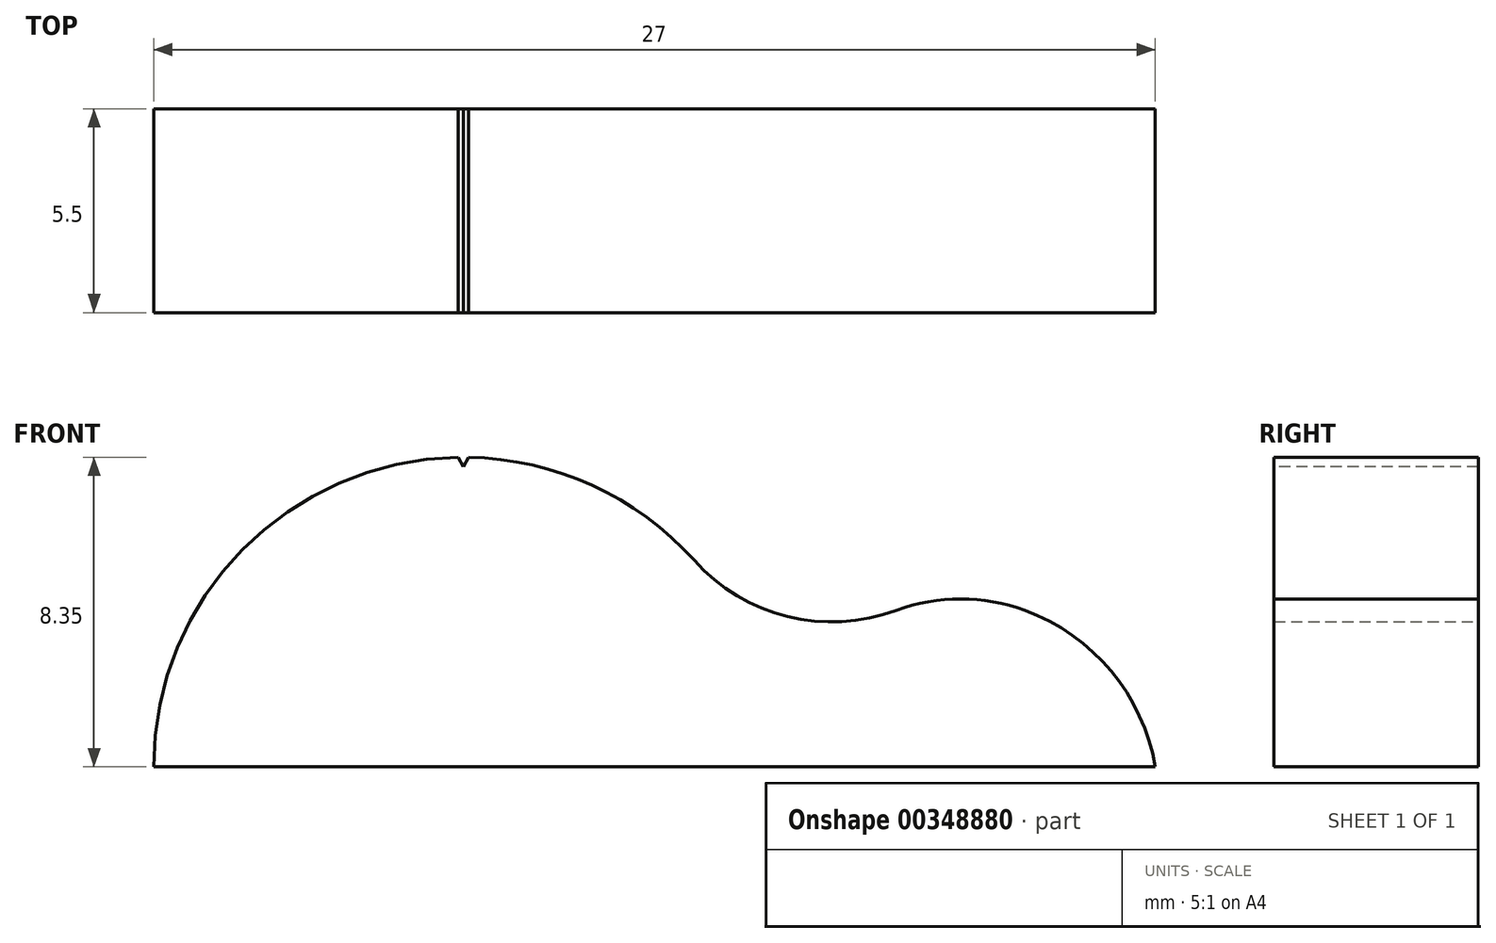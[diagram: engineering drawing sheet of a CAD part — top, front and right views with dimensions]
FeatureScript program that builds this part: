
annotation { "Feature Type Name" : "Feature", "Feature Type Description" : "" }
export const myFeature = defineFeature(function(context is Context, id is Id, definition is map)
    precondition{}
    {
        {
            var Q0;
            Q0=qCreatedBy(makeId("Front.planeOp"),FACE);
            var sketch = newSketch(context, id + "F0", { "sketchPlane" : qUnion([Q0])});
            skLineSegment(sketch, "E0", {"start": v(0, 0) * mm, "end": v(-27, 0) * mm});
            skArc(sketch, "E1", {"start": v(-27, 0) * mm, "mid": v(-21.63, 7.8) * mm, "end": v(-12.43, 5.57) * mm});
            skArc(sketch, "E2", {"start": v(-12.43, 5.57) * mm, "mid": v(-9.91, 4.06) * mm, "end": v(-6.98, 4.22) * mm});
            skArc(sketch, "E3", {"start": v(-3.51, 4.22) * mm, "mid": v(-5.25, 4.53) * mm, "end": v(-6.98, 4.22) * mm});
            skArc(sketch, "E4", {"start": v(0, 0) * mm, "mid": v(-1.2, 2.58) * mm, "end": v(-3.51, 4.22) * mm});
            skSolve(sketch);
        }
        {
            var Q0;
            Q0=qSketchRegion(id+"F0",true);
            extrude(context, id + "F1", {"entities" : qUnion([Q0]), "depth" : 5.5 * mm});
        }
        {
            var Q0;
            Q0=makeQuery(id+"F1.opExtrude","CAP_FACE",FACE,{"disambiguationData":[OSD([sQuery(id+"F0.wireOp",EDGE,"E0"),sQuery(id+"F0.wireOp",EDGE,"E1"),sQuery(id+"F0.wireOp",EDGE,"E2"),sQuery(id+"F0.wireOp",EDGE,"E3"),sQuery(id+"F0.wireOp",EDGE,"E4")])],"isStart":false});
            var sketch = newSketch(context, id + "F2", { "sketchPlane" : qUnion([Q0])});
            skArc(sketch, "E5.0", {"start": v(-18.8, 8.35) * mm, "mid": v(-18.65, 8.35) * mm, "end": v(-18.5, 8.35) * mm});
            skLineSegment(sketch, "E6", {"start": v(-18.65, 0) * mm, "end": v(-18.65, 8.35) * mm, "construction": true});
            skLineSegment(sketch, "E7", {"start": v(-18.65, 8.1) * mm, "end": v(-18.5, 8.35) * mm});
            skLineSegment(sketch, "E8", {"start": v(-18.65, 8.1) * mm, "end": v(-18.8, 8.35) * mm});
            skPoint(sketch, "E9.orphan", {"position": v(-12.43, 5.57) * mm});
            skPoint(sketch, "E10.orphan", {"position": v(-27, 0) * mm});
            skSolve(sketch);
        }
        {
            var Q0;
            Q0=qSketchRegion(id+"F2",true);
            extrude(context, id + "F3", {"entities" : qUnion([Q0]), "operationType" : NewBodyOperationType.REMOVE, "endBound" : BoundingType.THROUGH_ALL, "oppositeDirection" : true, "depth" : 25 * mm});
        }
    });
